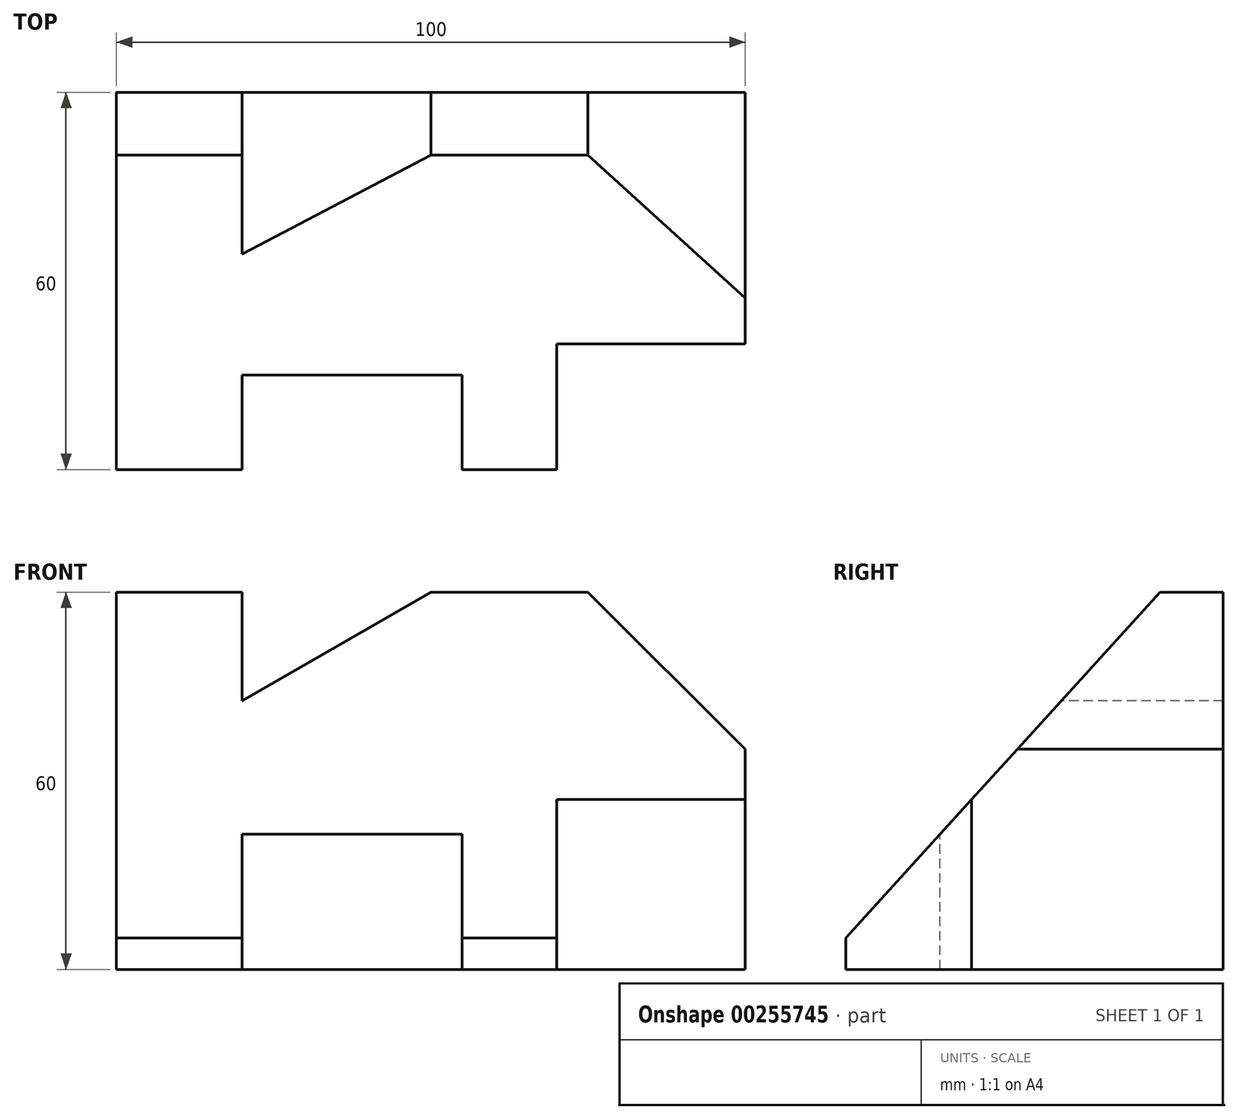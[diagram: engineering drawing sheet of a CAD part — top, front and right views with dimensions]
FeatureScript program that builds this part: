
annotation { "Feature Type Name" : "Feature", "Feature Type Description" : "" }
export const myFeature = defineFeature(function(context is Context, id is Id, definition is map)
    precondition{}
    {
        {
            var Q0;
            Q0=qCreatedBy(makeId("Top.planeOp"),FACE);
            var sketch = newSketch(context, id + "F0", { "sketchPlane" : qUnion([Q0])});
            skLineSegment(sketch, "E0", {"start": v(-55, 60) * mm, "end": v(-55, 0) * mm});
            skLineSegment(sketch, "E1", {"start": v(-55, 0) * mm, "end": v(-35, 0) * mm});
            skLineSegment(sketch, "E2", {"start": v(-35, 0) * mm, "end": v(-35, 15) * mm});
            skLineSegment(sketch, "E3", {"start": v(-35, 15) * mm, "end": v(0, 15) * mm});
            skLineSegment(sketch, "E4", {"start": v(0, 15) * mm, "end": v(0, 0) * mm});
            skLineSegment(sketch, "E5", {"start": v(0, 0) * mm, "end": v(15, 0) * mm});
            skLineSegment(sketch, "E6", {"start": v(15, 0) * mm, "end": v(15, 20) * mm});
            skLineSegment(sketch, "E7", {"start": v(15, 20) * mm, "end": v(45, 20) * mm});
            skLineSegment(sketch, "E8", {"start": v(45, 20) * mm, "end": v(45, 60) * mm});
            skLineSegment(sketch, "E9", {"start": v(45, 60) * mm, "end": v(-55, 60) * mm});
            skSolve(sketch);
        }
        {
            var Q0;
            Q0=makeQuery(id+"F0.imprint","IMPRINT",FACE,{"disambiguationData":[TD([[makeQuery(id+"F0.imprint","IMPRINT",EDGE,{"derivedFrom":sQuery(id+"F0.wireOp",EDGE,"E0")}),1.0]])]});
            extrude(context, id + "F1", {"entities" : qUnion([Q0]), "oppositeDirection" : true, "depth" : 60 * mm});
        }
        {
            var Q0;
            Q0=makeQuery(id+"F1.opExtrude","SWEPT_FACE",FACE,{"disambiguationData":[OSD([sQuery(id+"F0.wireOp",EDGE,"E0")])]});
            var sketch = newSketch(context, id + "F2", { "sketchPlane" : qUnion([Q0])});
            skLineSegment(sketch, "E10", {"start": v(-50, 0) * mm, "end": v(0, -55) * mm});
            skLineSegment(sketch, "E11", {"start": v(0, -55) * mm, "end": v(0, 0) * mm});
            skLineSegment(sketch, "E12", {"start": v(0, 0) * mm, "end": v(-50, 0) * mm});
            skSolve(sketch);
        }
        {
            var Q0;
            Q0=makeQuery(id+"F2.imprint","IMPRINT",FACE,{"disambiguationData":[TD([[makeQuery(id+"F2.imprint","IMPRINT",EDGE,{"derivedFrom":sQuery(id+"F2.wireOp",EDGE,"E10")}),1.0]])]});
            extrude(context, id + "F3", {"entities" : qUnion([Q0]), "operationType" : NewBodyOperationType.REMOVE, "endBound" : BoundingType.THROUGH_ALL, "oppositeDirection" : true, "depth" : 25 * mm});
        }
        {
            var Q0;
            Q0=qCreatedBy(makeId("Front.planeOp"),FACE);
            var sketch = newSketch(context, id + "F4", { "sketchPlane" : qUnion([Q0])});
            skLineSegment(sketch, "E13.0", {"start": v(-55, 0) * mm, "end": v(-35, 0) * mm});
            skPoint(sketch, "E14.0", {"position": v(-17.5, 0) * mm});
            skLineSegment(sketch, "E15.0.0", {"start": v(45, 0) * mm, "end": v(15, 0) * mm});
            skLineSegment(sketch, "E15.0.1", {"start": v(15, 0) * mm, "end": v(15, -60) * mm});
            skLineSegment(sketch, "E15.0.2", {"start": v(15, -60) * mm, "end": v(45, -60) * mm});
            skLineSegment(sketch, "E15.0.3", {"start": v(45, -60) * mm, "end": v(45, 0) * mm});
            skLineSegment(sketch, "E16.0.0", {"start": v(-35, 0) * mm, "end": v(-55, 0) * mm});
            skLineSegment(sketch, "E16.0.1", {"start": v(-55, 0) * mm, "end": v(-55, -60) * mm});
            skLineSegment(sketch, "E16.0.2", {"start": v(-55, -60) * mm, "end": v(-35, -60) * mm});
            skLineSegment(sketch, "E16.0.3", {"start": v(-35, -60) * mm, "end": v(-35, 0) * mm});
            skLineSegment(sketch, "E17.0.0", {"start": v(0, 0) * mm, "end": v(-35, 0) * mm});
            skLineSegment(sketch, "E17.0.1", {"start": v(-35, 0) * mm, "end": v(-35, -60) * mm});
            skLineSegment(sketch, "E17.0.2", {"start": v(-35, -60) * mm, "end": v(0, -60) * mm});
            skLineSegment(sketch, "E17.0.3", {"start": v(0, -60) * mm, "end": v(0, 0) * mm});
            skLineSegment(sketch, "E18", {"start": v(-55, -20) * mm, "end": v(-39.64, -20) * mm});
            skLineSegment(sketch, "E19", {"start": v(-39.64, -20) * mm, "end": v(-5, 0) * mm});
            skLineSegment(sketch, "E20", {"start": v(20, 0) * mm, "end": v(45, -25) * mm});
            skSolve(sketch);
        }
        {
            var Q0;
            {var subQ2=sQuery(id+"F4.wireOp",EDGE,"E16.0.0");Q0=makeQuery(id+"F4.imprint","IMPRINT",FACE,{"disambiguationData":[TD([[makeQuery(id+"F4.imprint","IMPRINT",EDGE,{"derivedFrom":subQ2}),1.0]])]});}
            var Q1;
            {var subQ1=sQuery(id+"F4.wireOp",EDGE,"E17.0.0");var subQ3=sQuery(id+"F4.wireOp",EDGE,"E19");var subQ4=makeQuery(id+"F4.imprint","INTERSECT",VERTEX,{"derivedFrom":[subQ1,subQ3]});Q1=makeQuery(id+"F4.imprint","IMPRINT",FACE,{"disambiguationData":[TD([[makeQuery(id+"F4.imprint","IMPRINT",EDGE,{"disambiguationData":[TD([[subQ4,1.0]])],"derivedFrom":subQ3}),1.0]])]});}
            var Q2;
            {var subQ3=sQuery(id+"F4.wireOp",EDGE,"E20");Q2=makeQuery(id+"F4.imprint","IMPRINT",FACE,{"disambiguationData":[TD([[makeQuery(id+"F4.imprint","IMPRINT",EDGE,{"derivedFrom":subQ3}),1.0]])]});}
            extrude(context, id + "F5", {"entities" : qUnion([Q0, Q1, Q2]), "operationType" : NewBodyOperationType.REMOVE, "endBound" : BoundingType.THROUGH_ALL, "oppositeDirection" : true, "depth" : 25 * mm});
        }
    });
